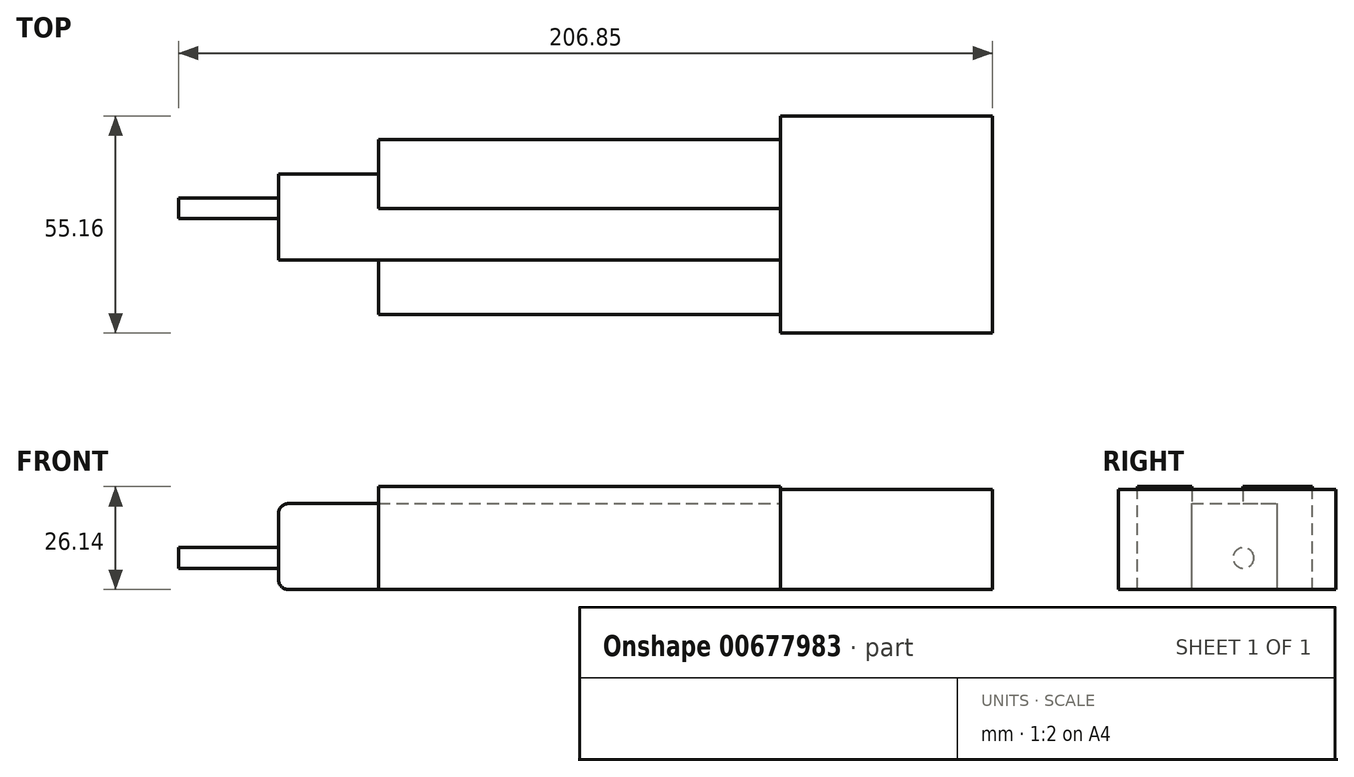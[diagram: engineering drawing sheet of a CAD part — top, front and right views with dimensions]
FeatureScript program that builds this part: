
annotation { "Feature Type Name" : "Feature", "Feature Type Description" : "" }
export const myFeature = defineFeature(function(context is Context, id is Id, definition is map)
    precondition{}
    {
        {
            var Q0;
            Q0=qCreatedBy(makeId("Top.planeOp"),FACE);
            var sketch = newSketch(context, id + "F0", { "sketchPlane" : qUnion([Q0])});
            skLineSegment(sketch, "E0.bottom", {"start": v(-37.38, 31.76) * mm, "end": v(16.56, 31.76) * mm});
            skLineSegment(sketch, "E0.top", {"start": v(-37.38, -23.4) * mm, "end": v(16.56, -23.4) * mm});
            skLineSegment(sketch, "E0.left", {"start": v(-37.38, 31.76) * mm, "end": v(-37.38, -23.4) * mm});
            skLineSegment(sketch, "E0.right", {"start": v(16.56, 31.76) * mm, "end": v(16.56, -23.4) * mm});
            skSolve(sketch);
        }
        {
            var Q0;
            Q0=makeQuery(id+"F0.imprint","IMPRINT",FACE,{"disambiguationData":[TD([[makeQuery(id+"F0.imprint","IMPRINT",EDGE,{"derivedFrom":sQuery(id+"F0.wireOp",EDGE,"E0.bottom")}),-1.0]])]});
            extrude(context, id + "F1", {"entities" : qUnion([Q0]), "depth" : 25.4 * mm, "offsetDistance" : 25.4 * mm});
        }
        {
            var Q0;
            Q0=makeQuery(id+"F1.opExtrude","SWEPT_FACE",FACE,{"disambiguationData":[OSD([sQuery(id+"F0.wireOp",EDGE,"E0.left")])]});
            var sketch = newSketch(context, id + "F2", { "sketchPlane" : qUnion([Q0])});
            skLineSegment(sketch, "E1.bottom", {"start": v(18.62, 5.03) * mm, "end": v(0, 5.03) * mm});
            skLineSegment(sketch, "E1.top", {"start": v(18.62, 21.82) * mm, "end": v(0, 21.82) * mm});
            skLineSegment(sketch, "E1.left", {"start": v(18.62, 5.03) * mm, "end": v(18.62, 21.82) * mm});
            skLineSegment(sketch, "E1.right", {"start": v(0, 5.03) * mm, "end": v(0, 21.82) * mm});
            skLineSegment(sketch, "E2.bottom", {"start": v(0, 5.03) * mm, "end": v(-25.78, 5.03) * mm});
            skLineSegment(sketch, "E2.top", {"start": v(0, 21.82) * mm, "end": v(-25.78, 21.82) * mm});
            skLineSegment(sketch, "E2.right", {"start": v(-25.78, 5.03) * mm, "end": v(-25.78, 21.82) * mm});
            skSolve(sketch);
        }
        {
            var Q0;
            Q0=makeQuery(id+"F2.imprint","IMPRINT",FACE,{"disambiguationData":[TD([[makeQuery(id+"F2.imprint","IMPRINT",EDGE,{"derivedFrom":sQuery(id+"F2.wireOp",EDGE,"E1.bottom")}),-1.0]])]});
            var Q1;
            Q1=makeQuery(id+"F2.imprint","IMPRINT",FACE,{"disambiguationData":[TD([[makeQuery(id+"F2.imprint","IMPRINT",EDGE,{"derivedFrom":sQuery(id+"F2.wireOp",EDGE,"E2.bottom")}),-1.0]])]});
            extrude(context, id + "F3", {"entities" : qUnion([Q0, Q1]), "operationType" : NewBodyOperationType.ADD, "depth" : 102.1 * mm, "offsetDistance" : 25.4 * mm});
        }
        {
            var Q0;
            Q0=makeQuery(id+"F3.opExtrude","SWEPT_FACE",FACE,{"disambiguationData":[OSD([sQuery(id+"F2.wireOp",EDGE,"E1.top"),sQuery(id+"F2.wireOp",EDGE,"E2.top")])]});
            var sketch = newSketch(context, id + "F4", { "sketchPlane" : qUnion([Q0])});
            skLineSegment(sketch, "E3.bottom", {"start": v(-139.49, -18.62) * mm, "end": v(-37.38, -18.62) * mm});
            skLineSegment(sketch, "E3.top", {"start": v(-139.49, -4.8) * mm, "end": v(-37.38, -4.8) * mm});
            skLineSegment(sketch, "E3.left", {"start": v(-139.49, -18.62) * mm, "end": v(-139.49, -4.8) * mm});
            skLineSegment(sketch, "E3.right", {"start": v(-37.38, -18.62) * mm, "end": v(-37.38, -4.8) * mm});
            skLineSegment(sketch, "E4.bottom", {"start": v(-139.49, 8.2) * mm, "end": v(-37.38, 8.2) * mm});
            skLineSegment(sketch, "E4.top", {"start": v(-139.49, 25.78) * mm, "end": v(-37.38, 25.78) * mm});
            skLineSegment(sketch, "E4.left", {"start": v(-139.49, 8.2) * mm, "end": v(-139.49, 25.78) * mm});
            skLineSegment(sketch, "E4.right", {"start": v(-37.38, 8.2) * mm, "end": v(-37.38, 25.78) * mm});
            skSolve(sketch);
        }
        {
            var Q0;
            Q0=makeQuery(id+"F4.imprint","IMPRINT",FACE,{"disambiguationData":[TD([[makeQuery(id+"F4.imprint","IMPRINT",EDGE,{"derivedFrom":sQuery(id+"F4.wireOp",EDGE,"E3.bottom")}),1.0]])]});
            var Q1;
            Q1=makeQuery(id+"F4.imprint","IMPRINT",FACE,{"disambiguationData":[TD([[makeQuery(id+"F4.imprint","IMPRINT",EDGE,{"derivedFrom":sQuery(id+"F4.wireOp",EDGE,"E4.bottom")}),1.0]])]});
            extrude(context, id + "F5", {"entities" : qUnion([Q0, Q1]), "operationType" : NewBodyOperationType.ADD, "depth" : 4.32 * mm, "offsetDistance" : 25.4 * mm});
        }
        {
            var Q0;
            Q0=makeQuery(id+"F3.opExtrude","SWEPT_FACE",FACE,{"disambiguationData":[OSD([sQuery(id+"F2.wireOp",EDGE,"E1.bottom"),sQuery(id+"F2.wireOp",EDGE,"E2.bottom")])]});
            var Q1;
            Q1=makeQuery(id+"F1.opExtrude","CAP_FACE",FACE,{"disambiguationData":[OSD([sQuery(id+"F0.wireOp",EDGE,"E0.bottom"),sQuery(id+"F0.wireOp",EDGE,"E0.top"),sQuery(id+"F0.wireOp",EDGE,"E0.left"),sQuery(id+"F0.wireOp",EDGE,"E0.right")])],"isStart":true});
            extrude(context, id + "F6", {"entities" : qUnion([Q0]), "operationType" : NewBodyOperationType.ADD, "endBound" : BoundingType.UP_TO_SURFACE, "depth" : 25.4 * mm, "endBoundEntityFace" : qUnion([Q1]), "offsetDistance" : 25.4 * mm});
        }
        {
            var Q0;
            {var subQ0=sQuery(id+"F2.wireOp",EDGE,"E2.bottom");var subQ1=sQuery(id+"F2.wireOp",EDGE,"E1.bottom");Q0=makeQuery(id+"F6.boolean.opBoolean","MERGE",FACE,{"derivedFrom":[makeQuery(id+"F5.boolean.opBoolean","MERGE",FACE,{"derivedFrom":[makeQuery(id+"F3.opExtrude","CAP_FACE",FACE,{"disambiguationData":[OSD([subQ1,sQuery(id+"F2.wireOp",EDGE,"E1.top"),sQuery(id+"F2.wireOp",EDGE,"E1.left"),subQ0,sQuery(id+"F2.wireOp",EDGE,"E2.top"),sQuery(id+"F2.wireOp",EDGE,"E2.right")])],"isStart":false}),makeQuery(id+"F5.opExtrude","SWEPT_FACE",FACE,{"disambiguationData":[OSD([sQuery(id+"F4.wireOp",EDGE,"E3.left")])]}),makeQuery(id+"F5.opExtrude","SWEPT_FACE",FACE,{"disambiguationData":[OSD([sQuery(id+"F4.wireOp",EDGE,"E4.left")])]})]}),makeQuery(id+"F6.opExtrude","SWEPT_FACE",FACE,{"disambiguationData":[OSD([subQ1,subQ0]),TDD([makeQuery(id+"F3.opExtrude","CAP_EDGE",EDGE,{"disambiguationData":[OSD([subQ1,subQ0])],"isStart":false})])]})]});}
            var sketch = newSketch(context, id + "F7", { "sketchPlane" : qUnion([Q0])});
            skPoint(sketch, "E5.oppositeSnap0", {"position": v(-16.99, 26.14) * mm});
            skLineSegment(sketch, "E5.bottom", {"start": v(4.8, 0) * mm, "end": v(-16.99, 0) * mm});
            skLineSegment(sketch, "E5.top", {"start": v(4.8, 21.82) * mm, "end": v(-16.99, 21.82) * mm});
            skLineSegment(sketch, "E5.left", {"start": v(4.8, 0) * mm, "end": v(4.8, 21.82) * mm});
            skLineSegment(sketch, "E5.right", {"start": v(-16.99, 0) * mm, "end": v(-16.99, 21.82) * mm});
            skSolve(sketch);
        }
        {
            var Q0;
            Q0=makeQuery(id+"F7.imprint","IMPRINT",FACE,{"disambiguationData":[TD([[makeQuery(id+"F7.imprint","IMPRINT",EDGE,{"derivedFrom":sQuery(id+"F7.wireOp",EDGE,"E5.bottom")}),1.0]])]});
            extrude(context, id + "F8", {"entities" : qUnion([Q0]), "operationType" : NewBodyOperationType.ADD, "depth" : 25.4 * mm, "offsetDistance" : 25.4 * mm});
        }
        {
            var Q0;
            Q0=makeQuery(id+"F8.opExtrude","CAP_FACE",FACE,{"disambiguationData":[OSD([sQuery(id+"F7.wireOp",EDGE,"E5.bottom"),sQuery(id+"F7.wireOp",EDGE,"E5.top"),sQuery(id+"F7.wireOp",EDGE,"E5.left"),sQuery(id+"F7.wireOp",EDGE,"E5.right")])],"isStart":false});
            var sketch = newSketch(context, id + "F9", { "sketchPlane" : qUnion([Q0])});
            skCircle(sketch, "E6", {"center": v(-8.33, 8.02) * mm, "radius": 2.64 * mm});
            skSolve(sketch);
        }
        {
            var Q0;
            Q0 = qSketchRegion(id + "F9", true);
            extrude(context, id + "F10", {"entities" : qUnion([Q0]), "operationType" : NewBodyOperationType.ADD, "depth" : 25.4 * mm, "offsetDistance" : 25.4 * mm});
        }
        {
            var Q0;
            Q0=makeQuery(id+"F8.opExtrude","CAP_EDGE",EDGE,{"disambiguationData":[OSD([sQuery(id+"F7.wireOp",EDGE,"E5.top")])],"isStart":false});
            fillet(context, id + "F11", {"entities" : qUnion([Q0]), "radius" : 2.54 * mm, "tangentPropagation" : true, "allowEdgeOverflow" : false});
        }
        {
            var Q0;
            Q0=makeQuery(id+"F8.opExtrude","CAP_EDGE",EDGE,{"disambiguationData":[OSD([sQuery(id+"F7.wireOp",EDGE,"E5.bottom")])],"isStart":false});
            fillet(context, id + "F12", {"entities" : qUnion([Q0]), "radius" : 2.54 * mm, "tangentPropagation" : true, "allowEdgeOverflow" : false});
        }
    });
